# Revit family: 0047137
name_source: partatom
category: Lighting Fixtures
revit_build: Autodesk Revit 2018 (Build: 20170223_1515(x64)
units: mm (PartAtom-declared; Revit-internal decimal feet)

## family parameters
Cut with Voids When Loaded = No
Host = Face
Light Source = Yes
OmniClass Number = 23.80.70.00
OmniClass Title = Lighting
Part Type = Normal
Room Calculation Point = No
Round Connector Dimension = Use Diameter
Shared = No

## types (1)
- 0047137 ST SRF WLL C IP54 2X140LM 2CCT WHT
    Apparent Load = 6 VA
    Assembly Code = D5020200
    AssetType = Fixed
    ClassificationName = Uniclass2015
    ClassificationValue = EF_70_80
    Color Filter = 16777215
    Cost = 0 $
    Default Elevation = 1219 mm
    Description = Exterior adjustable surface wall up and down light luminaire, white aluminium- RAL9016, 280lm, 5.8W, 48lm/W, 3000/4000K switchable CCT, CRI 80, IP54, IK05, 108x108x108mm, Class I
    Dimming Lamp Color Temperature Shift = <None>
    DocumentationLiterature = http://www.sylvania-lighting.com
    ElectricShockClassification = 48
    Emit Shape Visible in Rendering = No
    Emit from Circle Diameter = 610 mm
    Height = 108 mm  [stored 0.354331 ft]
    IfcExportAs = Class I
    IfcExportType = IfcLightFixtureType
    ImpactProtectionIndex = IfcLightFixtureType
    IngressProtection = IfcLightFixtureType
    InputNominalFrequency = Not Applicable
    InputVoltage = 0
    LampColourRenderingIndex = 16500
    LampColourTemperature = LED
    LampMacAdamStep = 80
    LampNominalLuminous = Not Applicable K
    Length = 108 mm  [stored 0.354331 ft]
    LightOutputRatio = LED
    LuminaireType = 0
    ManufacturerName = 48 lm/W
    Material = Feilo Sylvania
    Material_1_SYL = <By Category>
    Material_2_SYL = <By Category>
    Material_3_SYL = <By Category>
    Material_4_SYL = Glass, White, High Luminance
    Model = START Surface Wall Cube IP54 2x140lm 2CCT White
    ModelNumber = 0047137
    ModelReference = START Surface Wall Cube IP54 2x140lm 2CCT White
    Name = START Surface Wall Cube IP54 2x140lm 2CCT White
    NominalDepth = 0 mm  [stored 0 ft]
    NominalHeight = 0 mm  [stored 0 ft]
    NominalLength = 108 mm  [stored 0.354331 ft]
    Photometric Web File = 0047137.IES
    PowerConsumption = Lighting
    PowerFactor = 0
    Tilt Angle = 60.00°
    Type Image = <None>
    TypeName = START Surface Wall Cube IP54 2x140lm 2CCT White
    URL = 0.66
    Voltage = 0 V
    WarrantyDescription = http://www.sylvania-lighting.com
    Width = 108 mm  [stored 0.354331 ft]

note: [stored X ft] marks values corroborated as IEEE doubles in the binary element streams (Revit-internal decimal feet)

## geometry (parser evidence)
native form markers: Sweep x3
no freeform markers — native parametric forms only
